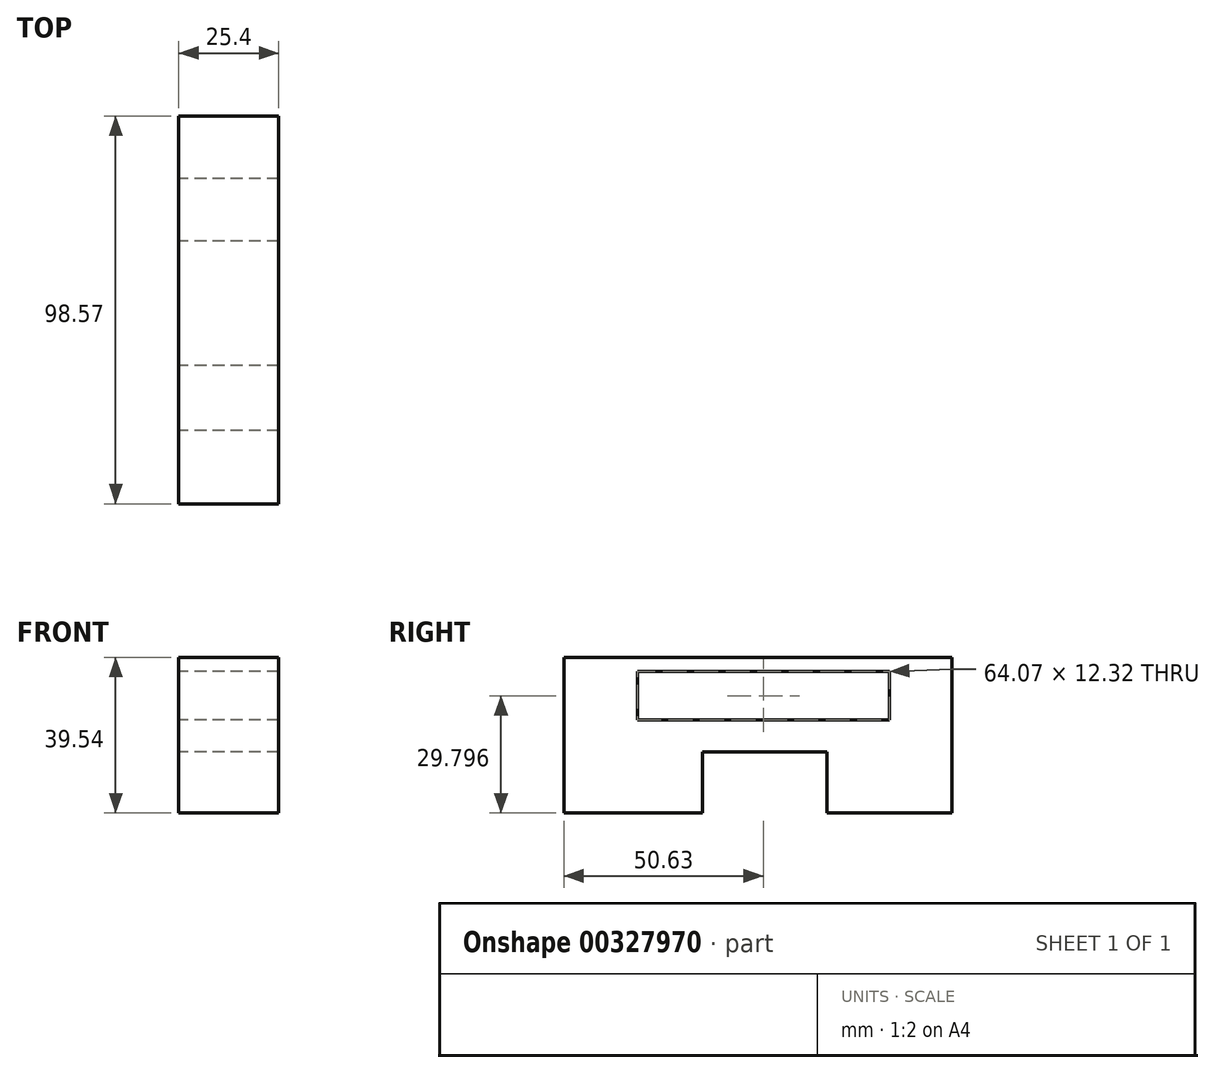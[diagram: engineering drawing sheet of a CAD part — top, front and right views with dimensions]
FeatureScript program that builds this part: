
annotation { "Feature Type Name" : "Feature", "Feature Type Description" : "" }
export const myFeature = defineFeature(function(context is Context, id is Id, definition is map)
    precondition{}
    {
        {
            var Q0;
            Q0=qCreatedBy(makeId("Right.planeOp"),FACE);
            var sketch = newSketch(context, id + "F0", { "sketchPlane" : qUnion([Q0])});
            skLineSegment(sketch, "E0.bottom", {"start": v(0, 0) * mm, "end": v(98.57, 0) * mm});
            skLineSegment(sketch, "E0.top", {"start": v(0, 39.54) * mm, "end": v(98.57, 39.54) * mm});
            skLineSegment(sketch, "E0.left", {"start": v(0, 0) * mm, "end": v(0, 39.54) * mm});
            skLineSegment(sketch, "E0.right", {"start": v(98.57, 0) * mm, "end": v(98.57, 39.54) * mm});
            skLineSegment(sketch, "E1.bottom", {"start": v(35.17, 0) * mm, "end": v(66.76, 0) * mm});
            skLineSegment(sketch, "E1.top", {"start": v(35.17, 15.57) * mm, "end": v(66.76, 15.57) * mm});
            skLineSegment(sketch, "E1.left", {"start": v(35.17, 0) * mm, "end": v(35.17, 15.57) * mm});
            skLineSegment(sketch, "E1.right", {"start": v(66.76, 0) * mm, "end": v(66.76, 15.57) * mm});
            skLineSegment(sketch, "E2", {"start": v(50.97, 15.57) * mm, "end": v(50.97, 0) * mm});
            skLineSegment(sketch, "E3.bottom", {"start": v(18.6, 35.96) * mm, "end": v(82.67, 35.96) * mm});
            skLineSegment(sketch, "E3.top", {"start": v(18.6, 23.63) * mm, "end": v(82.67, 23.63) * mm});
            skLineSegment(sketch, "E3.left", {"start": v(18.6, 35.96) * mm, "end": v(18.6, 23.63) * mm});
            skLineSegment(sketch, "E3.right", {"start": v(82.67, 35.96) * mm, "end": v(82.67, 23.63) * mm});
            skSolve(sketch);
        }
        {
            var Q0;
            Q0=makeQuery(id+"F0.imprint","IMPRINT",FACE,{"disambiguationData":[TD([[makeQuery(id+"F0.imprint","IMPRINT",EDGE,{"derivedFrom":sQuery(id+"F0.wireOp",EDGE,"E0.top")}),-1.0]])]});
            extrude(context, id + "F1", {"entities" : qUnion([Q0]), "depth" : 25.4 * mm});
        }
    });
